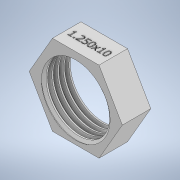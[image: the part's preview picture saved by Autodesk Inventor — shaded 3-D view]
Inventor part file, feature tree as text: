
AUTODESK INVENTOR PART (.ipt)
format: ipt  version: 2021.1 (Build 251245010, 245A)  size: 598,528 bytes
history: native  units: in
note: dims shown in document units (in); Inventor stores cm internally (conversion verified against a paired STEP export)
features: sketch x5, extrude x4, helix x1
ambient origin geometry x8: Origin, YZ Plane, XZ Plane, XY Plane, X Axis, Y Axis, Z Axis, Center Point
bodies: Solid1 (feature_tree)
feature tree (10):
  extrude  "Extrusion1"  Depth=0.125in
  helix  "Coil1"  [1 undecoded]
  extrude  "Extrusion2"  TaperAngle=60.0deg  [1 undecoded]
  extrude  "Extrusion3"  Depth=0.0072in
  extrude  "Extrusion4"  TaperAngle=120.0deg  [1 undecoded]
  sketch  "Sketch1"  dims[d0=1.1647in d1=0.125in d2=0.5in d3=0.0in]
  sketch  "Sketch2"  dims[d4=0.0072in d5=60.0deg]
  sketch  "Sketch3"  dims[d7=120.0deg d8=0.0072in]
  sketch  "Sketch4"  dims[d9=60.0deg d10=120.0deg]
  sketch  "Sketch5"  dims[d11=0.1in d12=0.05in d13=0.5824in d15=0.1in d16=0.7in d17=0.3937in d18=0.0in d19=90.0deg d20=90.0deg d21=0.0in d22=0.0in d23=0.5in d24=0.0in d25=0.6383in d26=0.05in d27=0.0in d28=0.05in d29=0.0in]
note: 3 required parameter values undecoded (feature->parameter linkage not recoverable at this tier; creation-order binding heuristic only, values carry confidence <= 0.55)
